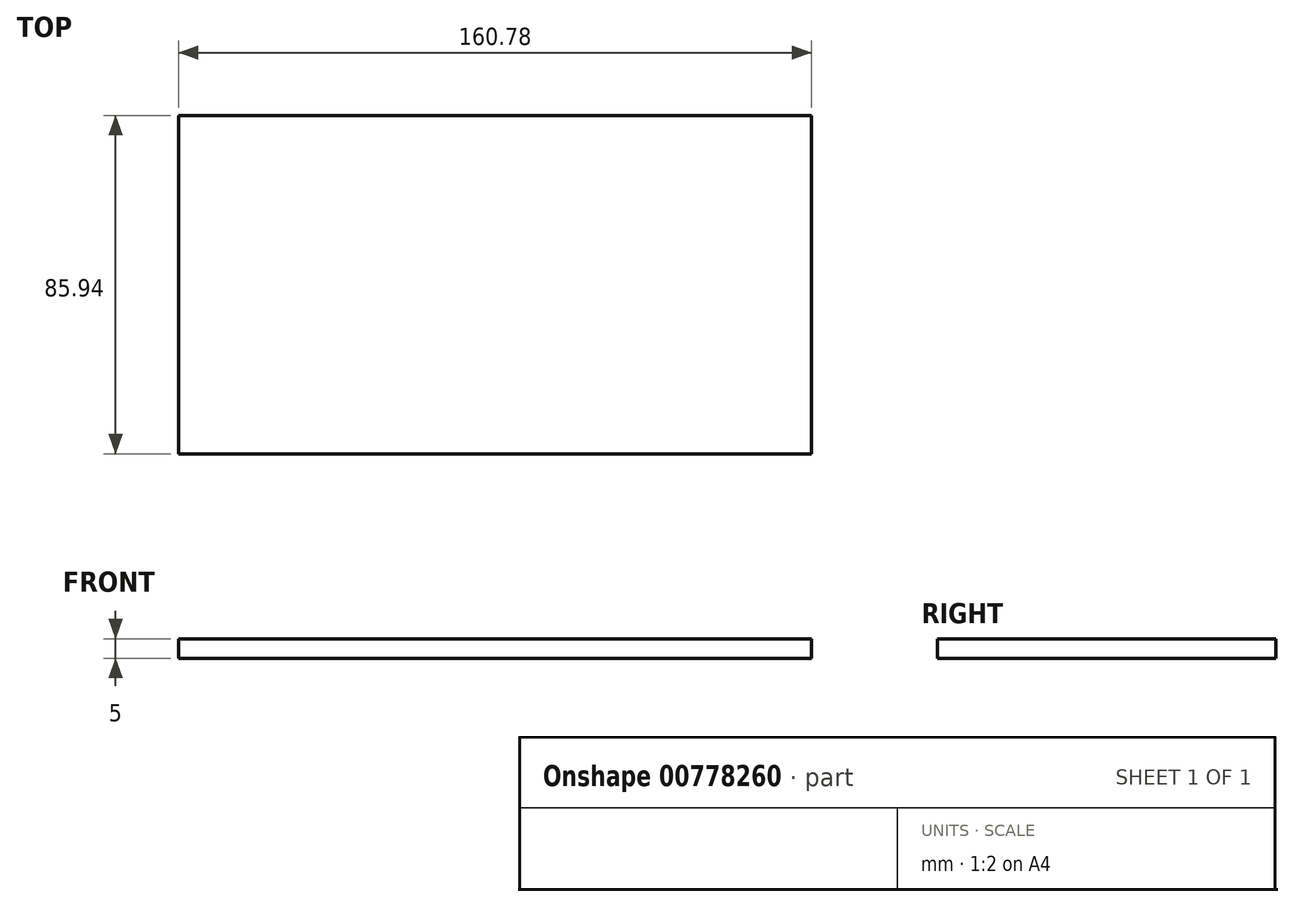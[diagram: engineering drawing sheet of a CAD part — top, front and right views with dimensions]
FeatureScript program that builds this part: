
annotation { "Feature Type Name" : "Feature", "Feature Type Description" : "" }
export const myFeature = defineFeature(function(context is Context, id is Id, definition is map)
    precondition{}
    {
        {
            var Q0;
            Q0=qCreatedBy(makeId("Top.planeOp"),FACE);
            var sketch = newSketch(context, id + "F0", { "sketchPlane" : qUnion([Q0])});
            skLineSegment(sketch, "E0.bottom", {"start": v(0, 0) * mm, "end": v(160.78, 0) * mm});
            skLineSegment(sketch, "E0.top", {"start": v(0, 85.94) * mm, "end": v(160.78, 85.94) * mm});
            skLineSegment(sketch, "E0.left", {"start": v(0, 0) * mm, "end": v(0, 85.94) * mm});
            skLineSegment(sketch, "E0.right", {"start": v(160.78, 0) * mm, "end": v(160.78, 85.94) * mm});
            skSolve(sketch);
        }
        {
            var Q0;
            Q0 = qSketchRegion(id + "F0", true);
            extrude(context, id + "F1", {"entities" : qUnion([Q0]), "depth" : 5 * mm, "offsetDistance" : 25.4 * mm});
        }
    });
